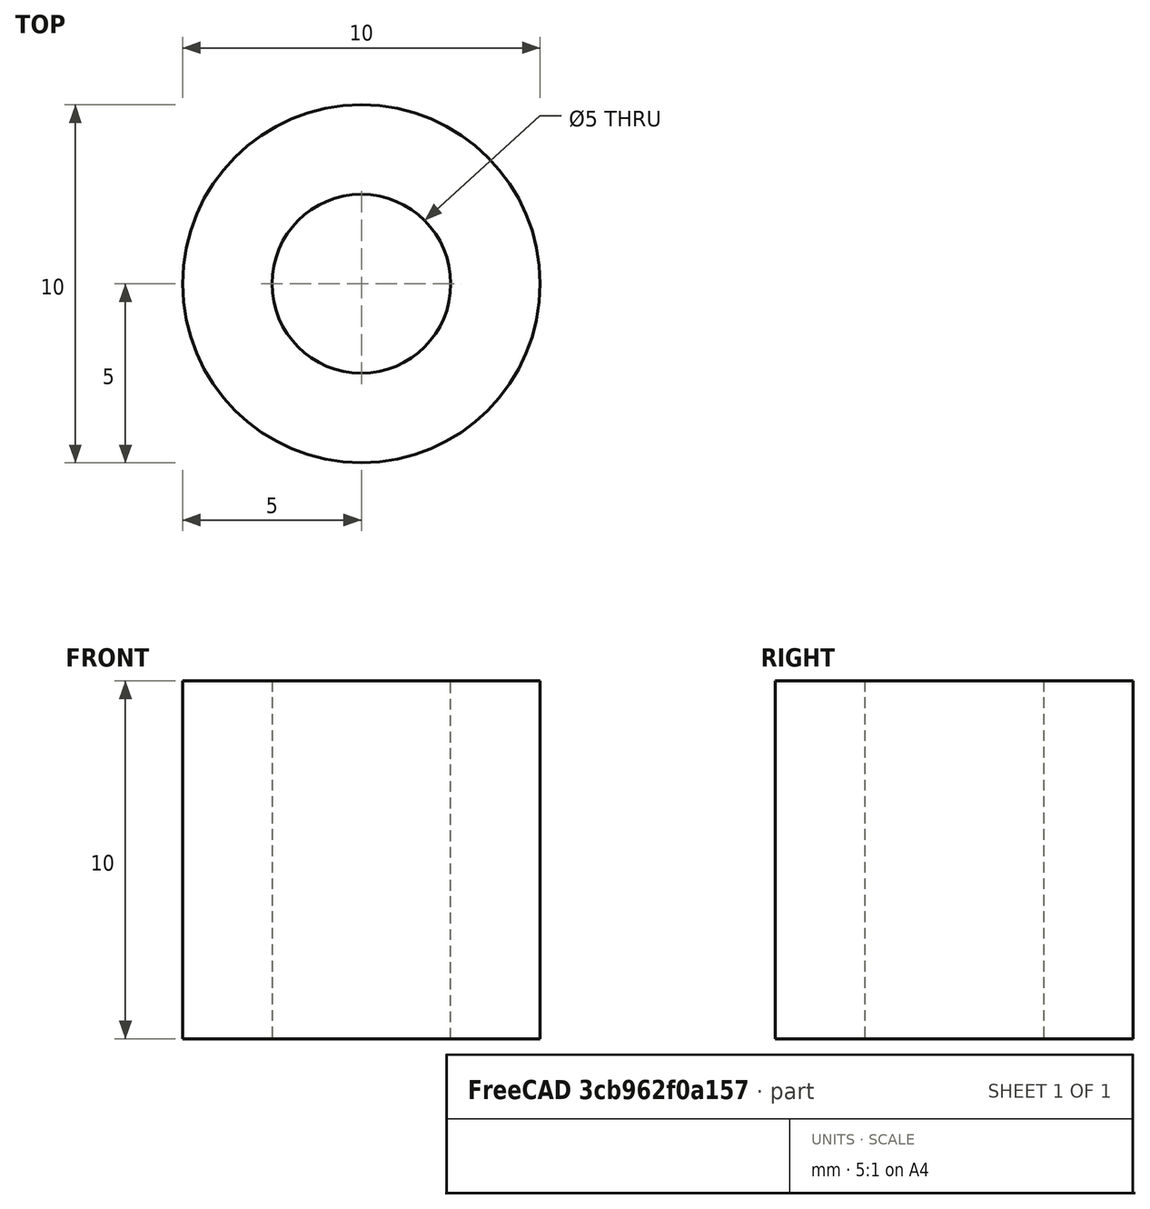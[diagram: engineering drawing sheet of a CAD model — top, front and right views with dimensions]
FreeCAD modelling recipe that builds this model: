
FCSTD DOCUMENT  (FreeCAD 0.19R24276 (Git))
Label: Axis_fix
License: All rights reserved
LicenseURL: http://en.wikipedia.org/wiki/All_rights_reserved
objects: Sketcher::SketchObject×1, PartDesign::Pad×1, PartDesign::Body×1
note: 4 computed .brp shape members not serialized (recipe doc carries the construction recipe); baked Part::Feature solids carry a one-line shape summary decoded from their .brp

FEATURE [Sketcher::SketchObject] Sketch
  FullyConstrained = true
  MapMode = 5
  Support = -> [XY_Plane]
  sketch-geometry (2):
    g0: Circle CenterX=0 CenterY=0 CenterZ=0 NormalX=0 NormalY=0 NormalZ=1 AngleXU=0 Radius=2.5
    g1: Circle CenterX=0 CenterY=0 CenterZ=0 NormalX=0 NormalY=0 NormalZ=1 AngleXU=0 Radius=5
  constraints (4):
    c: Coincident(g0,g-1)
    c: Diameter(g0) = 5
    c: Coincident(g1,g-1)
    c: Diameter(g1) = 10
FEATURE [PartDesign::Pad] Pad
  Direction = (1,1,1)
  Length = 10
  Length2 = 100
  Profile = -> Sketch
  Type = 0
FEATURE [PartDesign::Body] Body
  Group = -> [Sketch,Pad]
  Origin = -> Origin
  Tip = -> Pad
